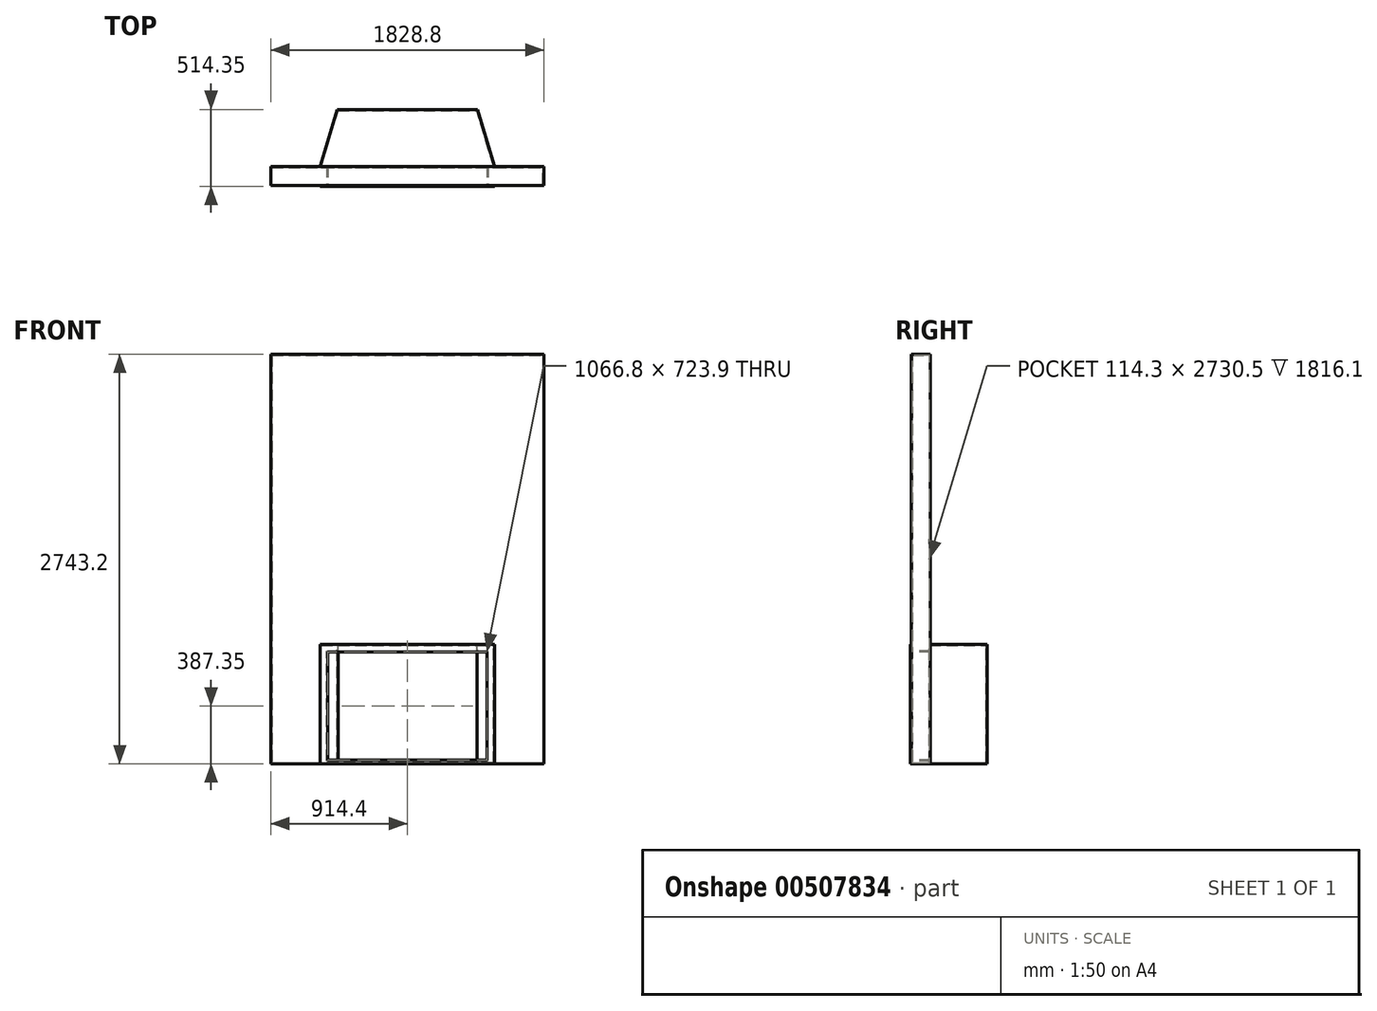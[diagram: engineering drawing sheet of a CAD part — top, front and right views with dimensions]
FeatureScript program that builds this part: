
annotation { "Feature Type Name" : "Feature", "Feature Type Description" : "" }
export const myFeature = defineFeature(function(context is Context, id is Id, definition is map)
    precondition{}
    {
        {
            var Q0;
            Q0=qCreatedBy(makeId("Front.planeOp"),FACE);
            var sketch = newSketch(context, id + "F0", { "sketchPlane" : qUnion([Q0])});
            skLineSegment(sketch, "E0.bottom", {"start": v(-914.4, 1371.6) * mm, "end": v(914.4, 1371.6) * mm});
            skLineSegment(sketch, "E0.top", {"start": v(-914.4, -1371.6) * mm, "end": v(914.4, -1371.6) * mm});
            skLineSegment(sketch, "E0.left", {"start": v(-914.4, 1371.6) * mm, "end": v(-914.4, -1371.6) * mm});
            skLineSegment(sketch, "E0.right", {"start": v(914.4, 1371.6) * mm, "end": v(914.4, -1371.6) * mm});
            skPoint(sketch, "E0.middle", {"position": v(0, 0) * mm});
            skSolve(sketch);
        }
        {
            var Q0;
            Q0 = qSketchRegion(id + "F0", true);
            extrude(context, id + "F1", {"entities" : qUnion([Q0]), "depth" : 127 * mm});
        }
        {
            var Q0;
            Q0=makeQuery(id+"F1.opExtrude","CAP_FACE",FACE,{"disambiguationData":[OSD([sQuery(id+"F0.wireOp",EDGE,"E0.bottom"),sQuery(id+"F0.wireOp",EDGE,"E0.top"),sQuery(id+"F0.wireOp",EDGE,"E0.left"),sQuery(id+"F0.wireOp",EDGE,"E0.right")])],"isStart":false});
            var sketch = newSketch(context, id + "F2", { "sketchPlane" : qUnion([Q0])});
            skLineSegment(sketch, "E1.bottom", {"start": v(-584.2, -1371.6) * mm, "end": v(584.2, -1371.6) * mm});
            skLineSegment(sketch, "E1.top", {"start": v(-533.4, -622.3) * mm, "end": v(533.4, -622.3) * mm});
            skLineSegment(sketch, "E1.left", {"start": v(-533.4, -1346.2) * mm, "end": v(-533.4, -622.3) * mm});
            skLineSegment(sketch, "E1.right", {"start": v(533.4, -1346.2) * mm, "end": v(533.4, -622.3) * mm});
            skLineSegment(sketch, "E2", {"start": v(0, -622.3) * mm, "end": v(0, 0) * mm, "construction": true});
            skLineSegment(sketch, "E3.0", {"start": v(584.2, -1371.6) * mm, "end": v(584.2, -571.5) * mm});
            skLineSegment(sketch, "E3.1", {"start": v(-584.2, -571.5) * mm, "end": v(584.2, -571.5) * mm});
            skLineSegment(sketch, "E3.2", {"start": v(-584.2, -1371.6) * mm, "end": v(-584.2, -571.5) * mm});
            skLineSegment(sketch, "E4.0", {"start": v(-533.4, -1346.2) * mm, "end": v(533.4, -1346.2) * mm});
            skSolve(sketch);
        }
        {
            var Q0;
            Q0=makeQuery(id+"F2.imprint","IMPRINT",FACE,{"disambiguationData":[TD([[makeQuery(id+"F2.imprint","IMPRINT",EDGE,{"derivedFrom":sQuery(id+"F2.wireOp",EDGE,"E1.top")}),-1.0]])]});
            var Q1;
            Q1=makeQuery(id+"F2.imprint","IMPRINT",FACE,{"disambiguationData":[TD([[makeQuery(id+"F2.imprint","IMPRINT",EDGE,{"derivedFrom":sQuery(id+"F2.wireOp",EDGE,"E1.bottom")}),1.0]])]});
            extrude(context, id + "F3", {"entities" : qUnion([Q0, Q1]), "operationType" : NewBodyOperationType.ADD, "oppositeDirection" : true, "depth" : 508 * mm, "hasSecondDirection" : true, "secondDirectionOppositeDirection" : false, "secondDirectionDepth" : 6.35 * mm});
        }
        {
            var Q0;
            {var subQ2=sQuery(id+"F2.wireOp",EDGE,"E3.1");Q0=makeQuery(id+"F3.boolean.opBoolean","SPLIT",FACE,{"disambiguationData":[TD([makeQuery(id+"F1.opExtrude","CAP_FACE",FACE,{"disambiguationData":[OSD([sQuery(id+"F0.wireOp",EDGE,"E0.bottom"),sQuery(id+"F0.wireOp",EDGE,"E0.top"),sQuery(id+"F0.wireOp",EDGE,"E0.left"),sQuery(id+"F0.wireOp",EDGE,"E0.right")])],"isStart":true})])],"derivedFrom":makeQuery(id+"F3.opExtrude","SWEPT_FACE",FACE,{"disambiguationData":[OSD([subQ2])]})});}
            var sketch = newSketch(context, id + "F4", { "sketchPlane" : qUnion([Q0])});
            skLineSegment(sketch, "E5", {"start": v(-584.2, 381) * mm, "end": v(-584.2, 0) * mm});
            skLineSegment(sketch, "E6", {"start": v(-584.2, 0) * mm, "end": v(-469.9, 381) * mm});
            skLineSegment(sketch, "E7", {"start": v(-469.9, 381) * mm, "end": v(-584.2, 381) * mm});
            skLineSegment(sketch, "E8", {"start": v(469.9, 381) * mm, "end": v(584.2, 381) * mm});
            skLineSegment(sketch, "E9", {"start": v(584.2, 381) * mm, "end": v(584.2, 0) * mm});
            skLineSegment(sketch, "E10", {"start": v(584.2, 0) * mm, "end": v(469.9, 381) * mm});
            skSolve(sketch);
        }
        {
            var Q0;
            Q0 = qSketchRegion(id + "F4", true);
            extrude(context, id + "F5", {"entities" : qUnion([Q0]), "operationType" : NewBodyOperationType.REMOVE, "endBound" : BoundingType.THROUGH_ALL, "oppositeDirection" : true, "depth" : 25.4 * mm});
        }
        {
            var Q0;
            Q0=makeQuery(id+"F3.opExtrude","CAP_FACE",FACE,{"disambiguationData":[OSD([sQuery(id+"F2.wireOp",EDGE,"E1.bottom"),sQuery(id+"F2.wireOp",EDGE,"E3.0"),sQuery(id+"F2.wireOp",EDGE,"E3.1"),sQuery(id+"F2.wireOp",EDGE,"E3.2")])],"isStart":true});
            var sketch = newSketch(context, id + "F6", { "sketchPlane" : qUnion([Q0])});
            skLineSegment(sketch, "E11.0", {"start": v(-533.4, -1346.2) * mm, "end": v(-533.4, -622.3) * mm});
            skLineSegment(sketch, "E11.1", {"start": v(-533.4, -622.3) * mm, "end": v(533.4, -622.3) * mm});
            skLineSegment(sketch, "E11.2", {"start": v(-533.4, -1346.2) * mm, "end": v(533.4, -1346.2) * mm});
            skLineSegment(sketch, "E11.3", {"start": v(533.4, -1346.2) * mm, "end": v(533.4, -622.3) * mm});
            skSolve(sketch);
        }
        {
            var Q0;
            Q0 = qSketchRegion(id + "F6", true);
            extrude(context, id + "F7", {"entities" : qUnion([Q0]), "operationType" : NewBodyOperationType.REMOVE, "oppositeDirection" : true, "depth" : 133.35 * mm});
        }
        {
            var Q0;
            Q0=makeQuery(id+"F7.boolean.opBoolean","COPY",FACE,{"derivedFrom":makeQuery(id+"F7.opExtrude","CAP_FACE",FACE,{"disambiguationData":[OSD([sQuery(id+"F6.wireOp",EDGE,"E11.0"),sQuery(id+"F6.wireOp",EDGE,"E11.1"),sQuery(id+"F6.wireOp",EDGE,"E11.2"),sQuery(id+"F6.wireOp",EDGE,"E11.3")])],"isStart":false})});
            shell(context, id + "F8", {"entities" : qUnion([Q0]), "thickness" : 6.35 * mm});
        }
    });
